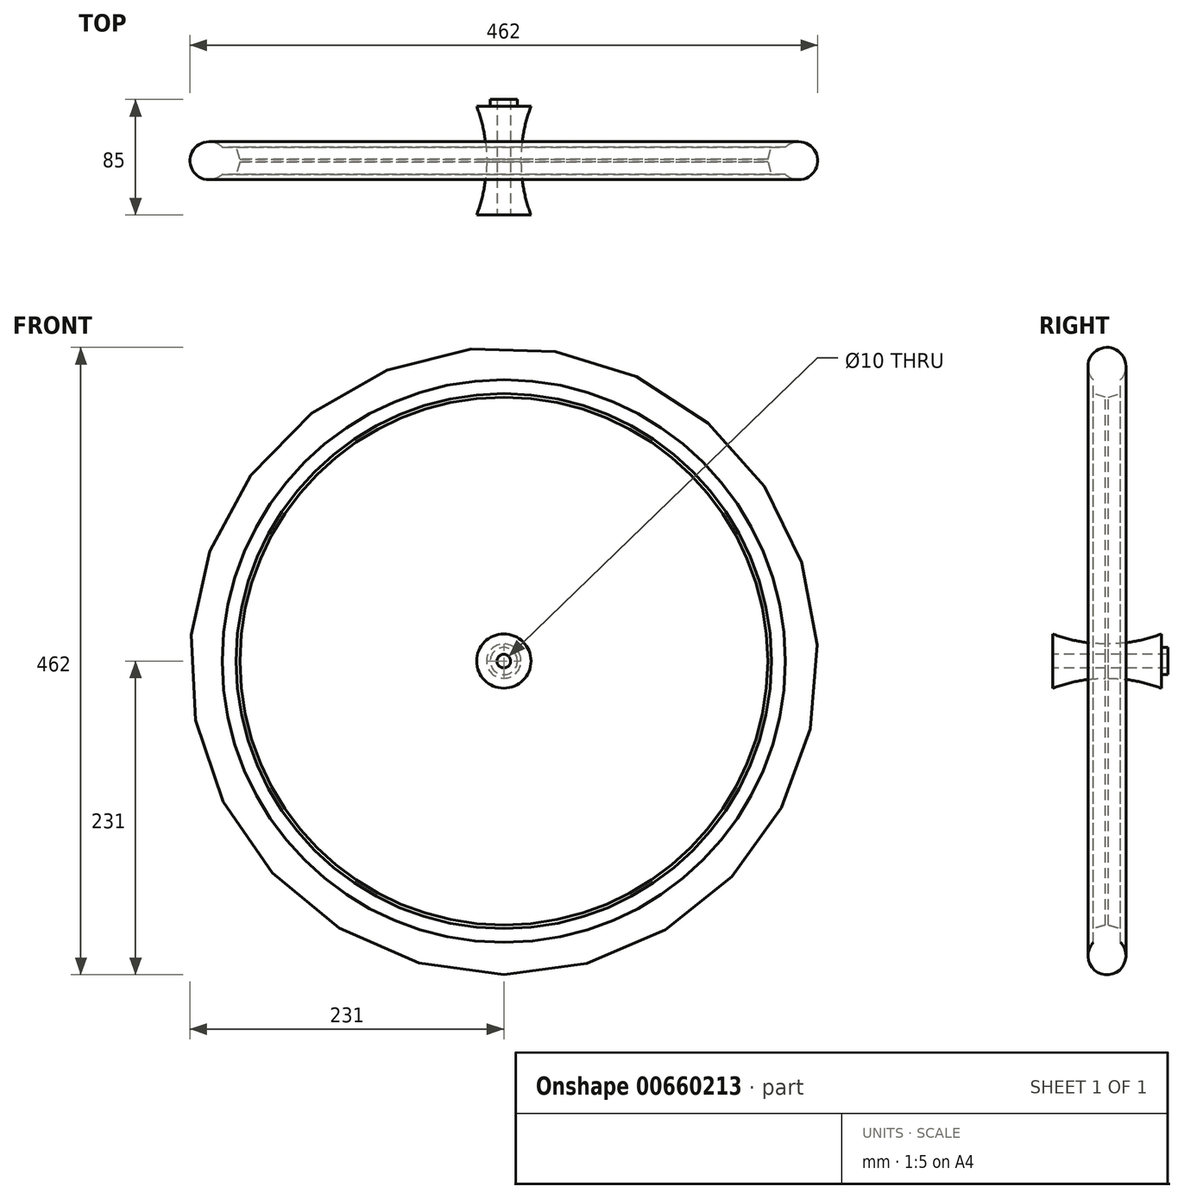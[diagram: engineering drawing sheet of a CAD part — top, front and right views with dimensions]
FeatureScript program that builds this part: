
annotation { "Feature Type Name" : "Feature", "Feature Type Description" : "" }
export const myFeature = defineFeature(function(context is Context, id is Id, definition is map)
    precondition{}
    {
        {
            var Q0;
            Q0=qCreatedBy(makeId("Right.planeOp"),FACE);
            var sketch = newSketch(context, id + "F0", { "sketchPlane" : qUnion([Q0])});
            skArc(sketch, "E0", {"start": v(10, 207.2) * mm, "mid": v(0, 231) * mm, "end": v(-10, 207.2) * mm});
            skLineSegment(sketch, "E1.left", {"start": v(-10, 197) * mm, "end": v(-10, 207.2) * mm});
            skLineSegment(sketch, "E1.right", {"start": v(10, 197) * mm, "end": v(10, 207.2) * mm});
            skLineSegment(sketch, "E2", {"start": v(-10, 197) * mm, "end": v(-1, 194.3) * mm});
            skLineSegment(sketch, "E3", {"start": v(1, 194.3) * mm, "end": v(10, 197) * mm});
            skPoint(sketch, "E1.bottom.end.orphan", {"position": v(0, 197) * mm});
            skLineSegment(sketch, "E4", {"start": v(-23.85, 0) * mm, "end": v(27.38, 0) * mm, "construction": true});
            skLineSegment(sketch, "E5.top", {"start": v(-40, 5) * mm, "end": v(40, 5) * mm});
            skLineSegment(sketch, "E5.left", {"start": v(-40, 20) * mm, "end": v(-40, 5) * mm});
            skLineSegment(sketch, "E5.right", {"start": v(40, 20) * mm, "end": v(40, 10) * mm});
            skArc(sketch, "E6", {"start": v(-40, 20) * mm, "mid": v(-20.83, 14.6) * mm, "end": v(-1, 12.66) * mm});
            skLineSegment(sketch, "E7.bottom", {"start": v(40, 5) * mm, "end": v(45, 5) * mm});
            skLineSegment(sketch, "E7.top", {"start": v(40, 10) * mm, "end": v(45, 10) * mm});
            skLineSegment(sketch, "E7.right", {"start": v(45, 5) * mm, "end": v(45, 10) * mm});
            skLineSegment(sketch, "E8.left", {"start": v(-1, 194.3) * mm, "end": v(-1, 12.66) * mm});
            skLineSegment(sketch, "E8.right", {"start": v(1, 194.3) * mm, "end": v(1, 12.66) * mm});
            skArc(sketch, "E9.trimOffspring", {"start": v(1, 12.66) * mm, "mid": v(20.83, 14.6) * mm, "end": v(40, 20) * mm});
            skSolve(sketch);
        }
        {
            var Q0;
            Q0=makeQuery(id+"F0.imprint","IMPRINT",FACE,{"disambiguationData":[TD([[makeQuery(id+"F0.imprint","IMPRINT",EDGE,{"derivedFrom":sQuery(id+"F0.wireOp",EDGE,"E0")}),1.0]])]});
            var Q1;
            Q1=makeQuery(id+"F0.imprint","IMPRINT",FACE,{"disambiguationData":[TD([[makeQuery(id+"F0.imprint","IMPRINT",EDGE,{"derivedFrom":sQuery(id+"F0.wireOp",EDGE,"E5.top")}),1.0]])]});
            var Q2;
            Q2=sQuery(id+"F0.wireOp",EDGE,"E4");
            revolve(context, id + "F1", {"surfaceOperationType" : NewSurfaceOperationType.NEW, "entities" : qUnion([Q0, Q1]), "axis" : qUnion([Q2]), "revolveType" : RevolveType.FULL});
        }
    });
